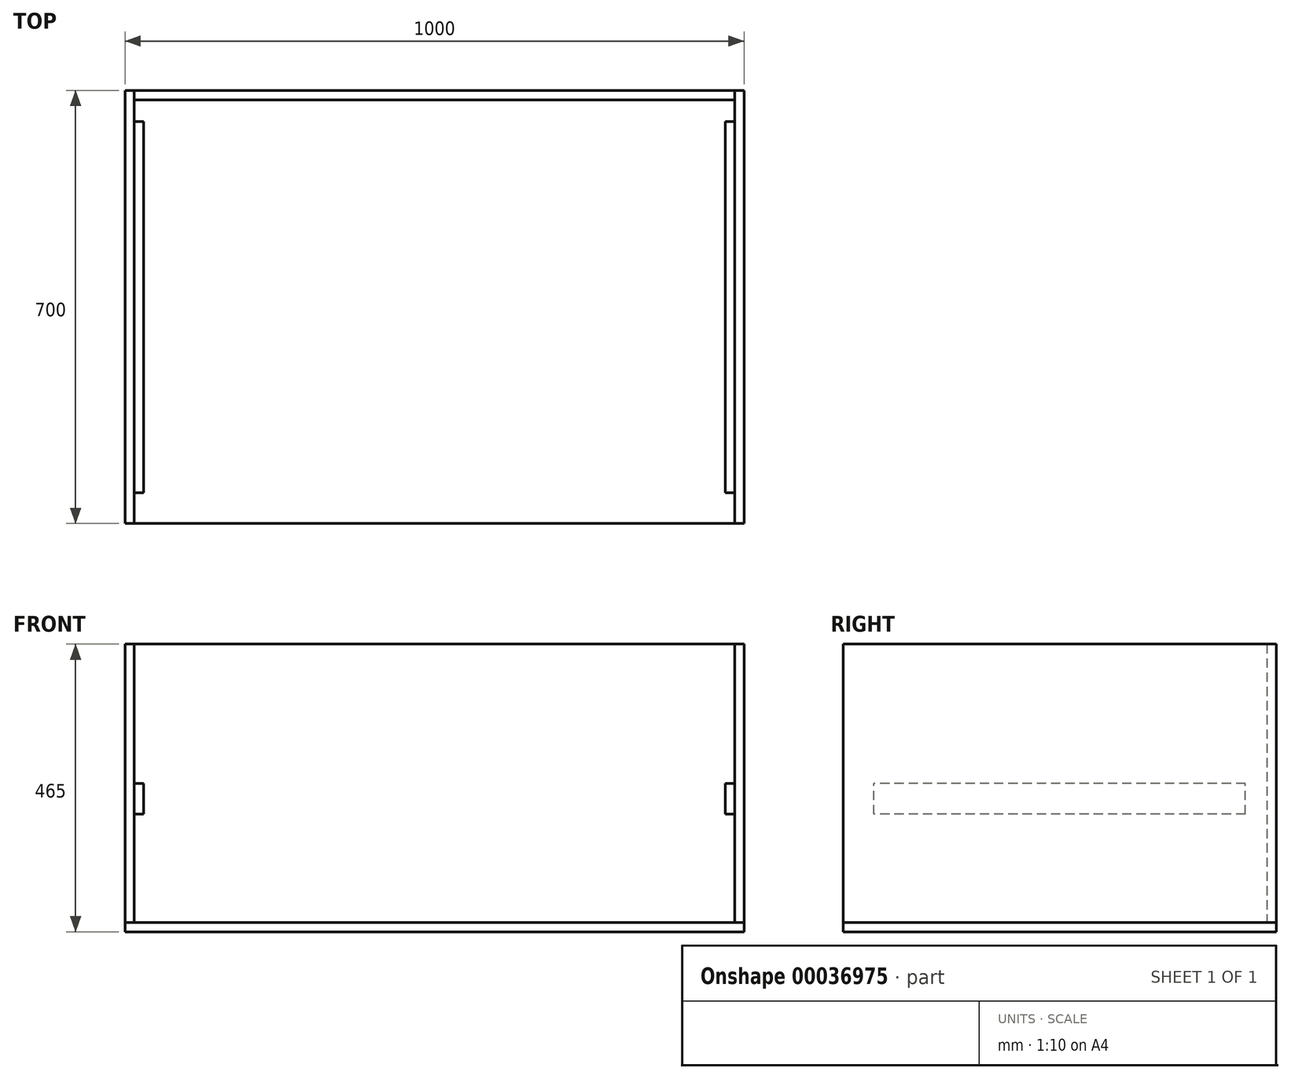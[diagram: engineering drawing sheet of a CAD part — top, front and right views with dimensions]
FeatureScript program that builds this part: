
annotation { "Feature Type Name" : "Feature", "Feature Type Description" : "" }
export const myFeature = defineFeature(function(context is Context, id is Id, definition is map)
    precondition{}
    {
        {
            var Q0;
            Q0=qCreatedBy(makeId("Top.planeOp"),FACE);
            var sketch = newSketch(context, id + "F0", { "sketchPlane" : qUnion([Q0])});
            skLineSegment(sketch, "E0.rect.bottom", {"start": v(500, -350) * mm, "end": v(-500, -350) * mm});
            skLineSegment(sketch, "E0.rect.top", {"start": v(500, 350) * mm, "end": v(-500, 350) * mm});
            skLineSegment(sketch, "E0.rect.left", {"start": v(500, -350) * mm, "end": v(500, 350) * mm});
            skLineSegment(sketch, "E0.rect.right", {"start": v(-500, -350) * mm, "end": v(-500, 350) * mm});
            skPoint(sketch, "E0.rect.middle", {"position": v(0, 0) * mm});
            skLineSegment(sketch, "E1.0", {"start": v(-485, -350) * mm, "end": v(-485, 335) * mm});
            skLineSegment(sketch, "E1.1", {"start": v(485, 335) * mm, "end": v(-485, 335) * mm});
            skLineSegment(sketch, "E1.2", {"start": v(485, -350) * mm, "end": v(485, 335) * mm});
            skLineSegment(sketch, "E2", {"start": v(485, 335) * mm, "end": v(485, 350) * mm});
            skLineSegment(sketch, "E3", {"start": v(-485, 335) * mm, "end": v(-485, 350) * mm});
            skSolve(sketch);
        }
        {
            var Q0;
            {var subQ2=sQuery(id+"F0.wireOp",EDGE,"E0.rect.right");Q0=makeQuery(id+"F0.imprint","IMPRINT",FACE,{"disambiguationData":[TD([[makeQuery(id+"F0.imprint","IMPRINT",EDGE,{"derivedFrom":subQ2}),-1.0]])]});}
            extrude(context, id + "F1", {"entities" : qUnion([Q0]), "depth" : 450 * mm});
        }
        {
            var Q0;
            Q0=makeQuery(id+"F0.imprint","IMPRINT",FACE,{"disambiguationData":[TD([[makeQuery(id+"F0.imprint","IMPRINT",EDGE,{"derivedFrom":sQuery(id+"F0.wireOp",EDGE,"E1.1")}),-1.0]])]});
            extrude(context, id + "F2", {"entities" : qUnion([Q0]), "depth" : 450 * mm});
        }
        {
            var Q0;
            {var subQ2=sQuery(id+"F0.wireOp",EDGE,"E0.rect.left");Q0=makeQuery(id+"F0.imprint","IMPRINT",FACE,{"disambiguationData":[TD([[makeQuery(id+"F0.imprint","IMPRINT",EDGE,{"derivedFrom":subQ2}),1.0]])]});}
            extrude(context, id + "F3", {"entities" : qUnion([Q0]), "depth" : 450 * mm});
        }
        {
            var Q0;
            {var subQ2=sQuery(id+"F0.wireOp",EDGE,"E0.rect.right");Q0=makeQuery(id+"F0.imprint","IMPRINT",FACE,{"disambiguationData":[TD([[makeQuery(id+"F0.imprint","IMPRINT",EDGE,{"derivedFrom":subQ2}),-1.0]])]});}
            var Q1;
            {var subQ1=sQuery(id+"F0.wireOp",EDGE,"E1.0");Q1=makeQuery(id+"F0.imprint","IMPRINT",FACE,{"disambiguationData":[TD([[makeQuery(id+"F0.imprint","IMPRINT",EDGE,{"derivedFrom":subQ1}),-1.0]])]});}
            var Q2;
            Q2=makeQuery(id+"F0.imprint","IMPRINT",FACE,{"disambiguationData":[TD([[makeQuery(id+"F0.imprint","IMPRINT",EDGE,{"derivedFrom":sQuery(id+"F0.wireOp",EDGE,"E1.1")}),-1.0]])]});
            var Q3;
            {var subQ2=sQuery(id+"F0.wireOp",EDGE,"E0.rect.left");Q3=makeQuery(id+"F0.imprint","IMPRINT",FACE,{"disambiguationData":[TD([[makeQuery(id+"F0.imprint","IMPRINT",EDGE,{"derivedFrom":subQ2}),1.0]])]});}
            var Q4;
            Q4=sQuery(id+"F0.wireOp",EDGE,"E0.rect.right");
            var Q5;
            Q5=sQuery(id+"F0.wireOp",EDGE,"E0.rect.bottom");
            var Q6;
            Q6=sQuery(id+"F0.wireOp",EDGE,"E0.rect.top");
            var Q7;
            Q7=sQuery(id+"F0.wireOp",EDGE,"E0.rect.left");
            extrude(context, id + "F4", {"entities" : qUnion([Q0, Q1, Q2, Q3]), "surfaceEntities" : qUnion([Q4, Q5, Q6, Q7]), "oppositeDirection" : true, "depth" : 15 * mm});
        }
        {
            var Q0;
            Q0=makeQuery(id+"F0.imprint","IMPRINT",FACE,{"disambiguationData":[TD([[makeQuery(id+"F0.imprint","IMPRINT",EDGE,{"derivedFrom":sQuery(id+"F0.wireOp",EDGE,"85392c47-4620-41fa-a122-52f978c5a5460.MirrorCS")}),1.0]])]});
            var Q1;
            Q1=makeQuery(id+"F0.imprint","IMPRINT",FACE,{"disambiguationData":[TD([[makeQuery(id+"F0.imprint","IMPRINT",EDGE,{"derivedFrom":sQuery(id+"F0.wireOp",EDGE,"E1.1")}),-1.0]])]});
            extrude(context, id + "F5", {"entities" : qUnion([Q0, Q1]), "depth" : 450 * mm});
        }
        {
            var Q0;
            Q0=makeQuery(id+"F1.opExtrude","SWEPT_FACE",FACE,{"disambiguationData":[OSD([sQuery(id+"F0.wireOp",EDGE,"E1.0"),sQuery(id+"F0.wireOp",EDGE,"E3")])]});
            var sketch = newSketch(context, id + "F6", { "sketchPlane" : qUnion([Q0])});
            skLineSegment(sketch, "E4", {"start": v(0, 0) * mm, "end": v(0, 200) * mm});
            skPoint(sketch, "E4.endSnap0", {"position": v(0, 0) * mm});
            skLineSegment(sketch, "E5.rect.bottom", {"start": v(300, 175) * mm, "end": v(-300, 175) * mm});
            skLineSegment(sketch, "E5.rect.top", {"start": v(300, 225) * mm, "end": v(-300, 225) * mm});
            skLineSegment(sketch, "E5.rect.left", {"start": v(300, 175) * mm, "end": v(300, 225) * mm});
            skLineSegment(sketch, "E5.rect.right", {"start": v(-300, 175) * mm, "end": v(-300, 225) * mm});
            skPoint(sketch, "E5.rect.middle", {"position": v(0, 200) * mm});
            skSolve(sketch);
        }
        {
            var Q0;
            Q0=makeQuery(id+"F6.imprint","IMPRINT",FACE,{"disambiguationData":[TD([[makeQuery(id+"F6.imprint","IMPRINT",EDGE,{"derivedFrom":sQuery(id+"F6.wireOp",EDGE,"E5.rect.top")}),1.0]])]});
            extrude(context, id + "F7", {"entities" : qUnion([Q0]), "depth" : 15 * mm});
        }
        {
            var Q0;
            Q0=makeQuery(id+"F7.opExtrude","SWEPT_BODY",BODY,{"disambiguationData":[OSD([sQuery(id+"F6.wireOp",EDGE,"E5.rect.bottom"),sQuery(id+"F6.wireOp",EDGE,"E5.rect.top"),sQuery(id+"F6.wireOp",EDGE,"E5.rect.left"),sQuery(id+"F6.wireOp",EDGE,"E5.rect.right")])]});
            var Q1;
            Q1=qCreatedBy(makeId("Right.planeOp"),FACE);
            mirror(context, id + "F8", {"entities" : qUnion([Q0]), "mirrorPlane" : qUnion([Q1])});
        }
        {
            var Q0;
            {var subQ2=sQuery(id+"F0.wireOp",EDGE,"E0.rect.right");Q0=makeQuery(id+"F0.imprint","IMPRINT",FACE,{"disambiguationData":[TD([[makeQuery(id+"F0.imprint","IMPRINT",EDGE,{"derivedFrom":subQ2}),-1.0]])]});}
            extrude(context, id + "F9", {"entities" : qUnion([Q0]), "depth" : 450 * mm});
        }
        {
            var Q0;
            Q0=makeQuery(id+"F1.opExtrude","SWEPT_BODY",BODY,{"disambiguationData":[OSD([sQuery(id+"F0.wireOp",EDGE,"E0.rect.bottom"),sQuery(id+"F0.wireOp",EDGE,"E0.rect.top"),sQuery(id+"F0.wireOp",EDGE,"E0.rect.right"),sQuery(id+"F0.wireOp",EDGE,"E1.0"),sQuery(id+"F0.wireOp",EDGE,"E3")])]});
            deleteBodies(context, id + "F10", {"entities" : qUnion([Q0])});
        }
        {
            var Q0;
            Q0=makeQuery(id+"F2.opExtrude","SWEPT_BODY",BODY,{"disambiguationData":[OSD([sQuery(id+"F0.wireOp",EDGE,"E0.rect.top"),sQuery(id+"F0.wireOp",EDGE,"E1.1"),sQuery(id+"F0.wireOp",EDGE,"E2"),sQuery(id+"F0.wireOp",EDGE,"E3")])]});
            deleteBodies(context, id + "F11", {"entities" : qUnion([Q0])});
        }
    });
